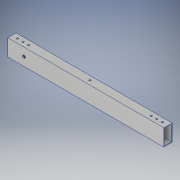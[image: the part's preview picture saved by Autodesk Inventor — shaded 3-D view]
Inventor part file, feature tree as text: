
AUTODESK INVENTOR PART (.ipt)
format: ipt  version: 2019 (Build 230136000, 136)  size: 158,208 bytes
history: native  units: mm
features: sketch x5, hole x3, extrude x2, other x1
ambient origin geometry x8: Origin, YZ Plane, XZ Plane, XY Plane, X Axis, Y Axis, Z Axis, Center Point
bodies: Body1 (feature_tree)
feature tree (11):
  other  "ソリッド1"
  extrude  "押し出し1"  Depth=30.0mm
  hole  "穴1"  [1 undecoded]
  extrude  "押し出し2"  Depth=280.0mm TaperAngle=0.0deg
  hole  "穴2"  [1 undecoded]
  hole  "穴3"  [1 undecoded]
  sketch  "スケッチ1"
  sketch  "スケッチ2"
  sketch  "スケッチ3"
  sketch  "スケッチ4"
  sketch  "スケッチ5"
note: 3 required parameter values undecoded (feature->parameter linkage not recoverable at this tier; creation-order binding heuristic only, values carry confidence <= 0.55)
